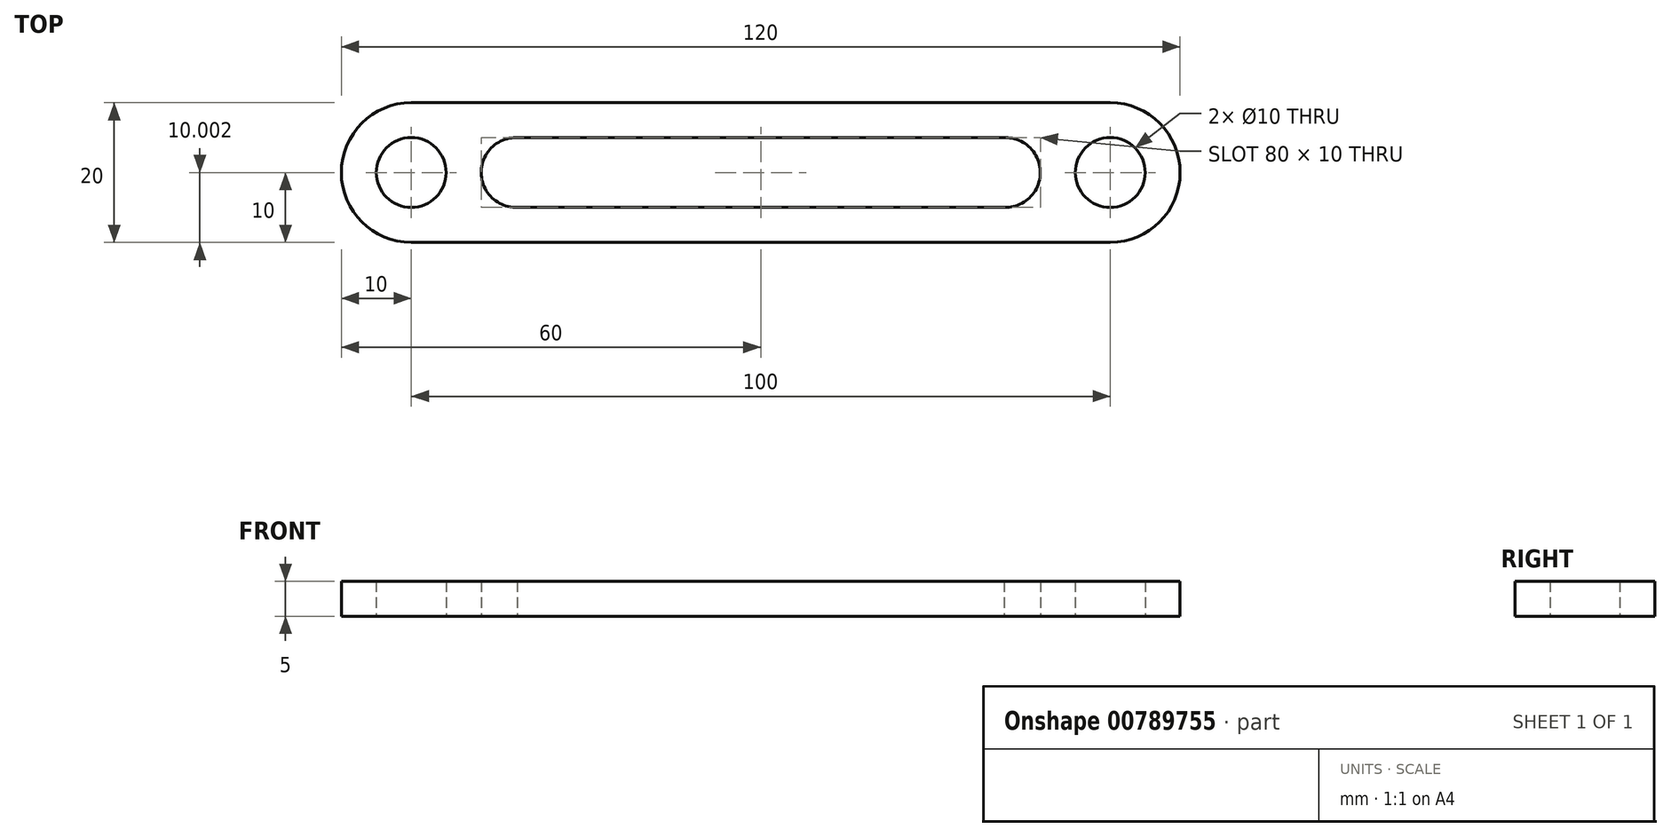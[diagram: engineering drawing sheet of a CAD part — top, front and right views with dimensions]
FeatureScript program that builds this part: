
annotation { "Feature Type Name" : "Feature", "Feature Type Description" : "" }
export const myFeature = defineFeature(function(context is Context, id is Id, definition is map)
    precondition{}
    {
        {
            var Q0;
            Q0=qCreatedBy(makeId("Top.planeOp"),FACE);
            var sketch = newSketch(context, id + "F0", { "sketchPlane" : qUnion([Q0])});
            skArc(sketch, "E0", {"start": v(0, 10) * mm, "mid": v(-10, 0) * mm, "end": v(0, -10) * mm});
            skArc(sketch, "E1", {"start": v(100, -10) * mm, "mid": v(110, 0) * mm, "end": v(100, 10) * mm});
            skLineSegment(sketch, "E2", {"start": v(0, 10) * mm, "end": v(100, 10) * mm});
            skLineSegment(sketch, "E3", {"start": v(0, -10) * mm, "end": v(100, -10) * mm});
            skCircle(sketch, "E4", {"center": v(0, 0) * mm, "radius": 5 * mm});
            skCircle(sketch, "E5", {"center": v(100, 0) * mm, "radius": 5 * mm});
            skArc(sketch, "E6", {"start": v(15, 5) * mm, "mid": v(10, -0.09) * mm, "end": v(15.18, -5) * mm});
            skArc(sketch, "E7", {"start": v(84.82, -5) * mm, "mid": v(90, -0.09) * mm, "end": v(85, 5) * mm});
            skLineSegment(sketch, "E8", {"start": v(15.18, -5) * mm, "end": v(85.18, -5) * mm});
            skLineSegment(sketch, "E9", {"start": v(85, 5) * mm, "end": v(15, 5) * mm});
            skSolve(sketch);
        }
        {
            var Q0;
            Q0=makeQuery(id+"F0.imprint","IMPRINT",FACE,{"disambiguationData":[TD([[makeQuery(id+"F0.imprint","IMPRINT",EDGE,{"derivedFrom":sQuery(id+"F0.wireOp",EDGE,"E0")}),1.0]])]});
            extrude(context, id + "F1", {"entities" : qUnion([Q0]), "depth" : 5 * mm, "offsetDistance" : 25 * mm});
        }
    });
